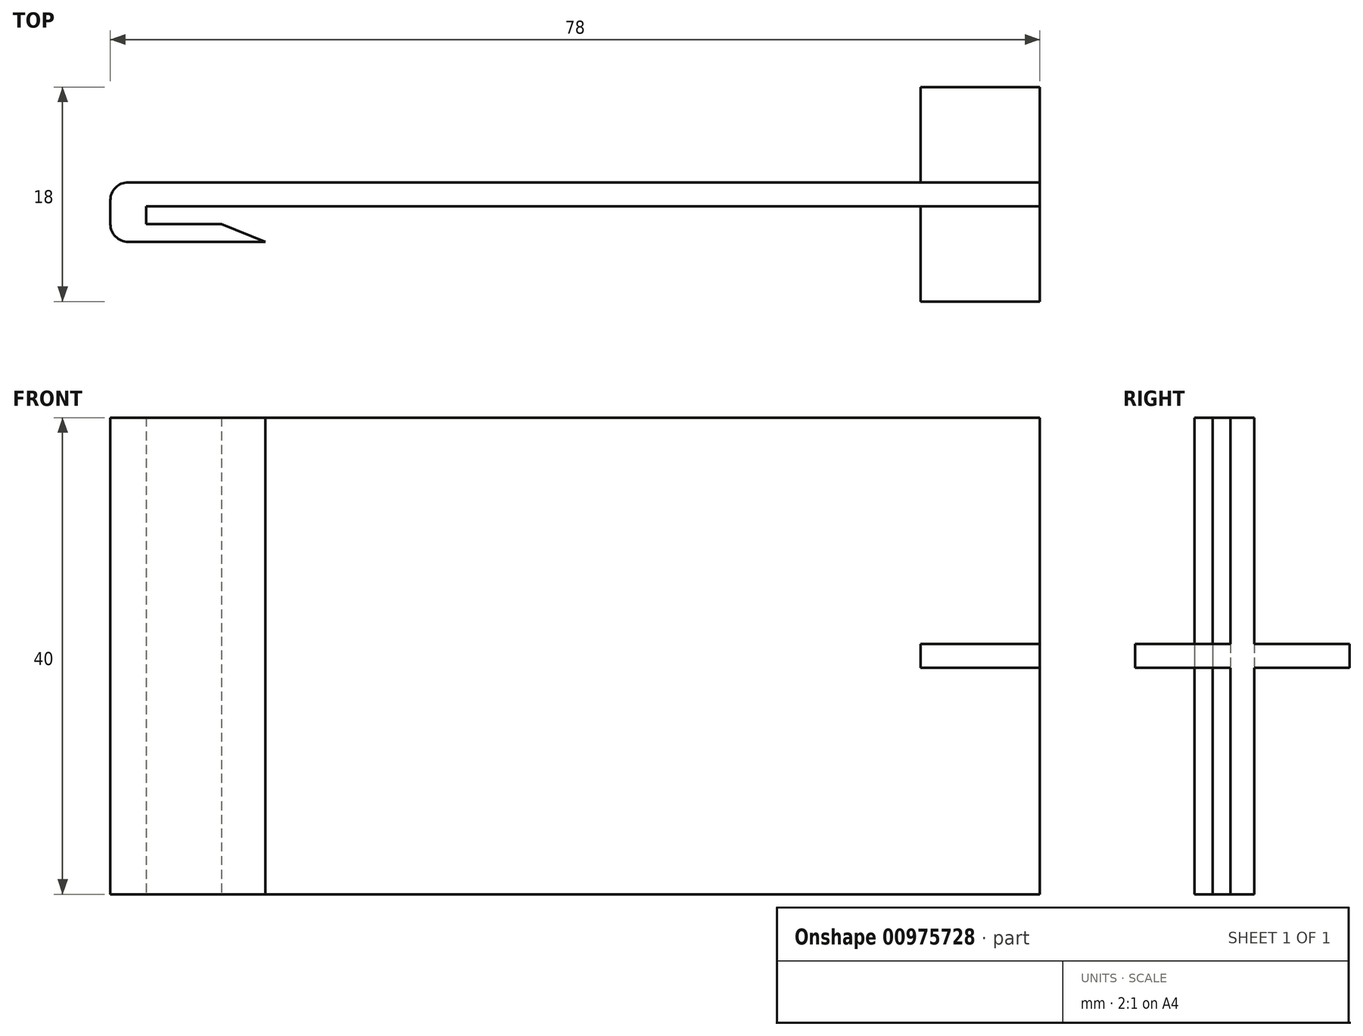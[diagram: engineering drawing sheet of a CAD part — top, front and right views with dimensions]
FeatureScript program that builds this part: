
annotation { "Feature Type Name" : "Feature", "Feature Type Description" : "" }
export const myFeature = defineFeature(function(context is Context, id is Id, definition is map)
    precondition{}
    {
        {
            var Q0;
            Q0=qCreatedBy(makeId("Top.planeOp"),FACE);
            var sketch = newSketch(context, id + "F0", { "sketchPlane" : qUnion([Q0])});
            skLineSegment(sketch, "E0", {"start": v(0, 0) * mm, "end": v(65, 0) * mm});
            skLineSegment(sketch, "E1", {"start": v(0, 0) * mm, "end": v(0, -1.5) * mm});
            skLineSegment(sketch, "E2", {"start": v(0, -1.5) * mm, "end": v(6.3, -1.5) * mm});
            skLineSegment(sketch, "E3.0", {"start": v(-3, 2) * mm, "end": v(65, 2) * mm});
            skLineSegment(sketch, "E4.0", {"start": v(-3, -3) * mm, "end": v(10, -3) * mm});
            skLineSegment(sketch, "E5.0", {"start": v(-3, 2) * mm, "end": v(-3, -3) * mm});
            skLineSegment(sketch, "E6", {"start": v(10, -3) * mm, "end": v(6.3, -1.5) * mm});
            skLineSegment(sketch, "E7", {"start": v(65, 2) * mm, "end": v(65, 0) * mm});
            skSolve(sketch);
        }
        {
            var Q0;
            Q0 = qSketchRegion(id + "F0", true);
            extrude(context, id + "F1", {"entities" : qUnion([Q0]), "endBound" : BoundingType.SYMMETRIC, "depth" : 40 * mm, "offsetDistance" : 25 * mm});
        }
        {
            var Q0;
            Q0=makeQuery(id+"F1.opExtrude","SWEPT_FACE",FACE,{"disambiguationData":[OSD([sQuery(id+"F0.wireOp",EDGE,"E7")])]});
            var sketch = newSketch(context, id + "F2", { "sketchPlane" : qUnion([Q0])});
            skLineSegment(sketch, "E8.0.0", {"start": v(0, -20) * mm, "end": v(2, -20) * mm});
            skLineSegment(sketch, "E8.0.1", {"start": v(2, -20) * mm, "end": v(2, 20) * mm});
            skLineSegment(sketch, "E8.0.2", {"start": v(2, 20) * mm, "end": v(0, 20) * mm});
            skLineSegment(sketch, "E8.0.3", {"start": v(0, 20) * mm, "end": v(0, -20) * mm});
            skLineSegment(sketch, "E9", {"start": v(2, 1) * mm, "end": v(10, 1) * mm});
            skLineSegment(sketch, "E10.0", {"start": v(2, -1) * mm, "end": v(10, -1) * mm});
            skLineSegment(sketch, "E11", {"start": v(10, 1) * mm, "end": v(10, -1) * mm});
            skLineSegment(sketch, "E12.MirrorCS", {"start": v(2, 1) * mm, "end": v(-8, 1) * mm});
            skLineSegment(sketch, "E13.MirrorCS", {"start": v(-8, 1) * mm, "end": v(-8, -1) * mm});
            skLineSegment(sketch, "E14.MirrorCS", {"start": v(2, -1) * mm, "end": v(-8, -1) * mm});
            skPoint(sketch, "E15.orphan", {"position": v(12, 1) * mm});
            skPoint(sketch, "E16.orphan", {"position": v(12, -1) * mm});
            skSolve(sketch);
        }
        {
            var Q0;
            Q0 = qSketchRegion(id + "F2", true);
            extrude(context, id + "F3", {"entities" : qUnion([Q0]), "operationType" : NewBodyOperationType.ADD, "depth" : 10 * mm, "offsetDistance" : 25 * mm});
        }
        {
            var Q0;
            Q0=makeQuery(id+"F1.opExtrude","SWEPT_EDGE",EDGE,{"disambiguationData":[OSD([sQuery(id+"F0.wireOp",EDGE,"E4.0"),sQuery(id+"F0.wireOp",EDGE,"E5.0")])]});
            var Q1;
            Q1=makeQuery(id+"F1.opExtrude","SWEPT_EDGE",EDGE,{"disambiguationData":[OSD([sQuery(id+"F0.wireOp",EDGE,"E3.0"),sQuery(id+"F0.wireOp",EDGE,"E5.0")])]});
            fillet(context, id + "F4", {"entities" : qUnion([Q0, Q1]), "radius" : 1.5 * mm, "tangentPropagation" : true, "allowEdgeOverflow" : false});
        }
    });
